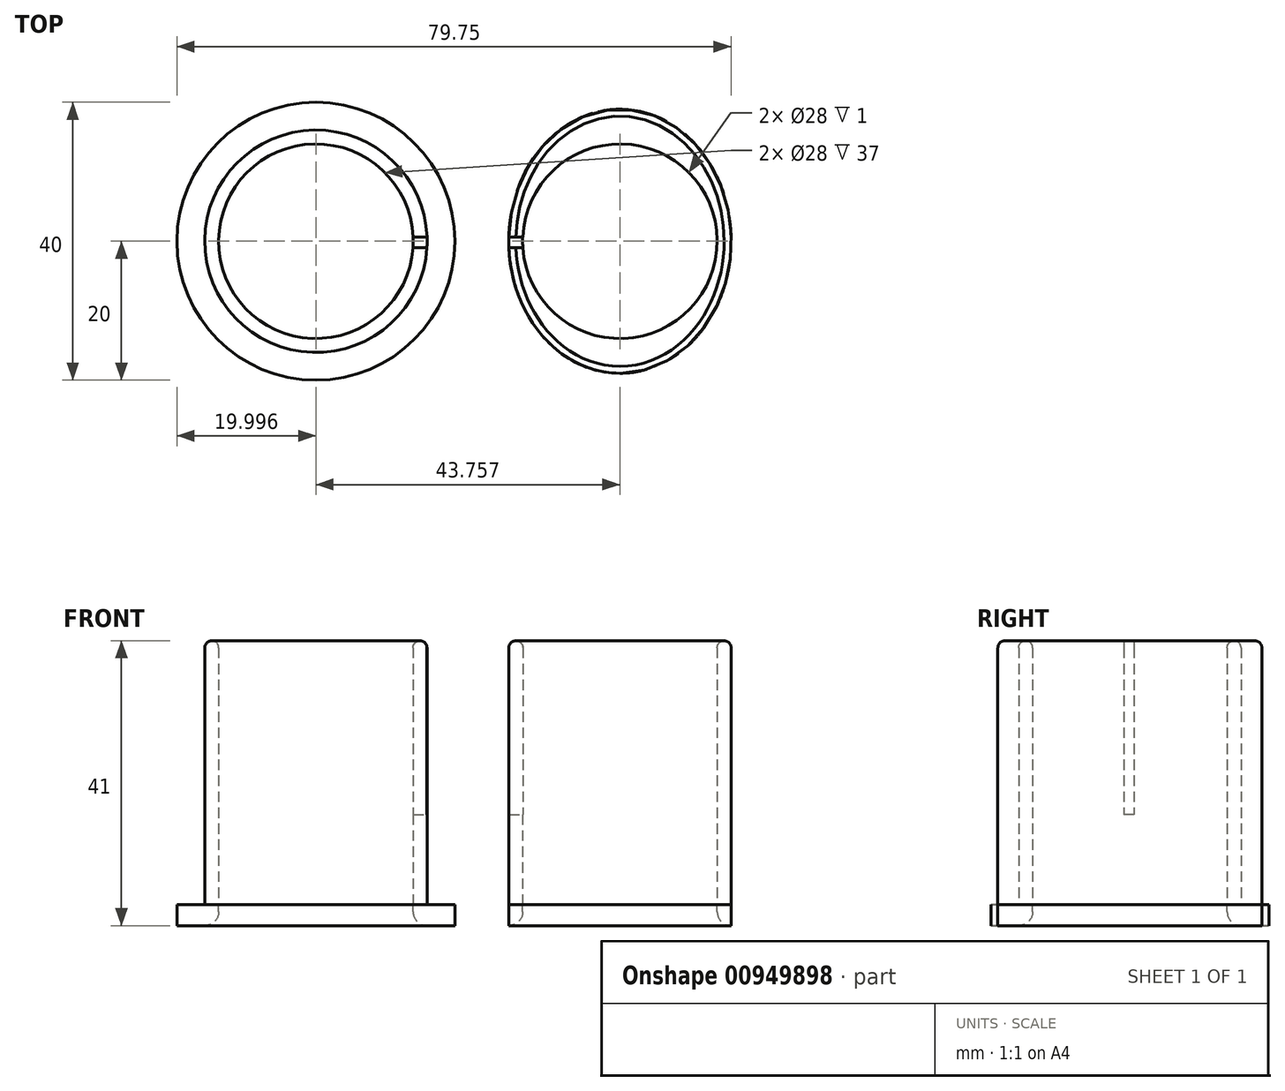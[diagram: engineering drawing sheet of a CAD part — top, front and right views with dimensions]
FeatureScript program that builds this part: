
annotation { "Feature Type Name" : "Feature", "Feature Type Description" : "" }
export const myFeature = defineFeature(function(context is Context, id is Id, definition is map)
    precondition{}
    {
        {
            var Q0;
            Q0=qCreatedBy(makeId("Top.planeOp"),FACE);
            var sketch = newSketch(context, id + "F0", { "sketchPlane" : qUnion([Q0])});
            skCircle(sketch, "E0", {"center": v(-22.7, 0) * mm, "radius": 16 * mm});
            skCircle(sketch, "E1", {"center": v(-22.7, 0) * mm, "radius": 14 * mm});
            skEllipse(sketch, "E2", {"center": v(21.05, 0) * mm, "majorRadius": 19 * mm, "minorRadius": 16 * mm, "majorAxis": v(0, -1)});
            skCircle(sketch, "E3", {"center": v(21.05, 0) * mm, "radius": 14 * mm});
            skFitSpline(sketch, "E4.0", {"points": [v(19, -22.92) * mm, v(21.05, -23.04) * mm, v(23.1, -22.92) * mm, v(25.77, -22.45) * mm, v(28.35, -21.52) * mm, v(30.75, -20.17) * mm, v(33.02, -18.55) * mm, v(35.52, -16.1) * mm, v(37.54, -13.19) * mm, v(38.84, -10.6) * mm, v(39.9, -7.92) * mm, v(40.63, -5.1) * mm, v(41, -2.2) * mm, v(41.08, 0) * mm, v(41, 2.2) * mm, v(40.63, 5.1) * mm, v(39.9, 7.92) * mm, v(38.84, 10.6) * mm, v(37.54, 13.19) * mm, v(35.52, 16.1) * mm, v(33.02, 18.55) * mm, v(30.75, 20.17) * mm, v(28.35, 21.52) * mm, v(25.77, 22.45) * mm, v(23.1, 22.92) * mm, v(21.05, 23.04) * mm, v(19, 22.92) * mm, v(16.33, 22.45) * mm, v(13.76, 21.52) * mm, v(11.35, 20.17) * mm, v(9.08, 18.55) * mm, v(6.58, 16.1) * mm, v(4.56, 13.19) * mm, v(3.26, 10.6) * mm, v(2.2, 7.92) * mm, v(1.48, 5.1) * mm, v(1.11, 2.2) * mm, v(1.02, 0) * mm, v(1.11, -2.2) * mm, v(1.48, -5.1) * mm, v(2.2, -7.92) * mm, v(3.26, -10.6) * mm, v(4.56, -13.19) * mm, v(6.58, -16.1) * mm, v(9.08, -18.55) * mm, v(11.35, -20.17) * mm, v(13.76, -21.52) * mm, v(16.33, -22.45) * mm, v(19, -22.92) * mm, v(21.05, -23.04) * mm, v(23.1, -22.92) * mm, v(19, -22.92) * mm]});
            skCircle(sketch, "E5.0", {"center": v(-22.7, 0) * mm, "radius": 20 * mm});
            skSolve(sketch);
        }
        {
            var Q0;
            Q0=makeQuery(id+"F0.imprint","IMPRINT",FACE,{"disambiguationData":[TD([[makeQuery(id+"F0.imprint","IMPRINT",EDGE,{"derivedFrom":sQuery(id+"F0.wireOp",EDGE,"E2")}),1.0]])]});
            var Q1;
            Q1=makeQuery(id+"F0.imprint","IMPRINT",FACE,{"disambiguationData":[TD([[makeQuery(id+"F0.imprint","IMPRINT",EDGE,{"derivedFrom":sQuery(id+"F0.wireOp",EDGE,"E0")}),1.0]])]});
            extrude(context, id + "F1", {"entities" : qUnion([Q0, Q1]), "depth" : 38 * mm, "offsetDistance" : 25 * mm});
        }
        {
            var Q0;
            Q0=makeQuery(id+"F1.opExtrude","CAP_EDGE",EDGE,{"disambiguationData":[OSD([sQuery(id+"F0.wireOp",EDGE,"E1")])],"isStart":false});
            var Q1;
            Q1=makeQuery(id+"F1.opExtrude","CAP_EDGE",EDGE,{"disambiguationData":[OSD([sQuery(id+"F0.wireOp",EDGE,"E0")])],"isStart":false});
            var Q2;
            Q2=makeQuery(id+"F1.opExtrude","CAP_EDGE",EDGE,{"disambiguationData":[OSD([sQuery(id+"F0.wireOp",EDGE,"E2")])],"isStart":false});
            var Q3;
            Q3=makeQuery(id+"F1.opExtrude","CAP_EDGE",EDGE,{"disambiguationData":[OSD([sQuery(id+"F0.wireOp",EDGE,"E3")])],"isStart":false});
            fillet(context, id + "F2", {"entities" : qUnion([Q0, Q1, Q2, Q3]), "radius" : 1 * mm, "tangentPropagation" : true, "allowEdgeOverflow" : false});
        }
        {
            var Q0;
            Q0=makeQuery(id+"F0.imprint","IMPRINT",FACE,{"disambiguationData":[TD([[makeQuery(id+"F0.imprint","IMPRINT",EDGE,{"derivedFrom":sQuery(id+"F0.wireOp",EDGE,"E0")}),1.0]])]});
            var Q1;
            Q1=makeQuery(id+"F0.imprint","IMPRINT",FACE,{"disambiguationData":[TD([[makeQuery(id+"F0.imprint","IMPRINT",EDGE,{"derivedFrom":sQuery(id+"F0.wireOp",EDGE,"E0")}),-1.0]])]});
            var Q2;
            Q2=makeQuery(id+"F0.imprint","IMPRINT",FACE,{"disambiguationData":[TD([[makeQuery(id+"F0.imprint","IMPRINT",EDGE,{"derivedFrom":sQuery(id+"F0.wireOp",EDGE,"E2")}),-1.0]])]});
            var Q3;
            Q3=makeQuery(id+"F0.imprint","IMPRINT",FACE,{"disambiguationData":[TD([[makeQuery(id+"F0.imprint","IMPRINT",EDGE,{"derivedFrom":sQuery(id+"F0.wireOp",EDGE,"E2")}),1.0]])]});
            extrude(context, id + "F3", {"entities" : qUnion([Q0, Q1, Q2, Q3]), "oppositeDirection" : true, "depth" : 3 * mm, "offsetDistance" : 25 * mm});
        }
        {
            var Q0;
            Q0=makeQuery(id+"F3.opExtrude","CAP_EDGE",EDGE,{"disambiguationData":[OSD([sQuery(id+"F0.wireOp",EDGE,"E1")])],"isStart":false});
            var Q1;
            Q1=makeQuery(id+"F3.opExtrude","CAP_EDGE",EDGE,{"disambiguationData":[OSD([sQuery(id+"F0.wireOp",EDGE,"E3")])],"isStart":false});
            fillet(context, id + "F4", {"entities" : qUnion([Q0, Q1]), "radius" : 2 * mm, "tangentPropagation" : true, "allowEdgeOverflow" : false});
        }
        {
            var Q0;
            Q0=makeQuery(id+"F2.opFillet","SPLIT",FACE,{"disambiguationData":[OD(0.0)],"derivedFrom":makeQuery(id+"F1.opExtrude","CAP_FACE",FACE,{"disambiguationData":[OSD([sQuery(id+"F0.wireOp",EDGE,"E2"),sQuery(id+"F0.wireOp",EDGE,"E3")])],"isStart":false})});
            cPlane(context, id + "F5", {"entities" : qUnion([Q0]), "cplaneType" : CPlaneType.OFFSET, "offset" : 0 * mm, "width" : 150 * mm, "height" : 150 * mm});
        }
        {
            var Q0;
            Q0=qCreatedBy(id+"F5.planeOp",FACE);
            var sketch = newSketch(context, id + "F6", { "sketchPlane" : qUnion([Q0])});
            skLineSegment(sketch, "E6.bottom", {"start": v(-10, -0.9) * mm, "end": v(10, -0.9) * mm});
            skLineSegment(sketch, "E6.top", {"start": v(-10, 0.6) * mm, "end": v(10, 0.6) * mm});
            skLineSegment(sketch, "E6.left", {"start": v(-10, -0.9) * mm, "end": v(-10, 0.6) * mm});
            skLineSegment(sketch, "E6.right", {"start": v(10, -0.9) * mm, "end": v(10, 0.6) * mm});
            skSolve(sketch);
        }
        {
            var Q0;
            Q0=makeQuery(id+"F6.imprint","IMPRINT",FACE,{"disambiguationData":[TD([[makeQuery(id+"F6.imprint","IMPRINT",EDGE,{"derivedFrom":sQuery(id+"F6.wireOp",EDGE,"E6.bottom")}),1.0]])]});
            extrude(context, id + "F7", {"entities" : qUnion([Q0]), "operationType" : NewBodyOperationType.REMOVE, "oppositeDirection" : true, "depth" : 25 * mm, "offsetDistance" : 25 * mm});
        }
    });
